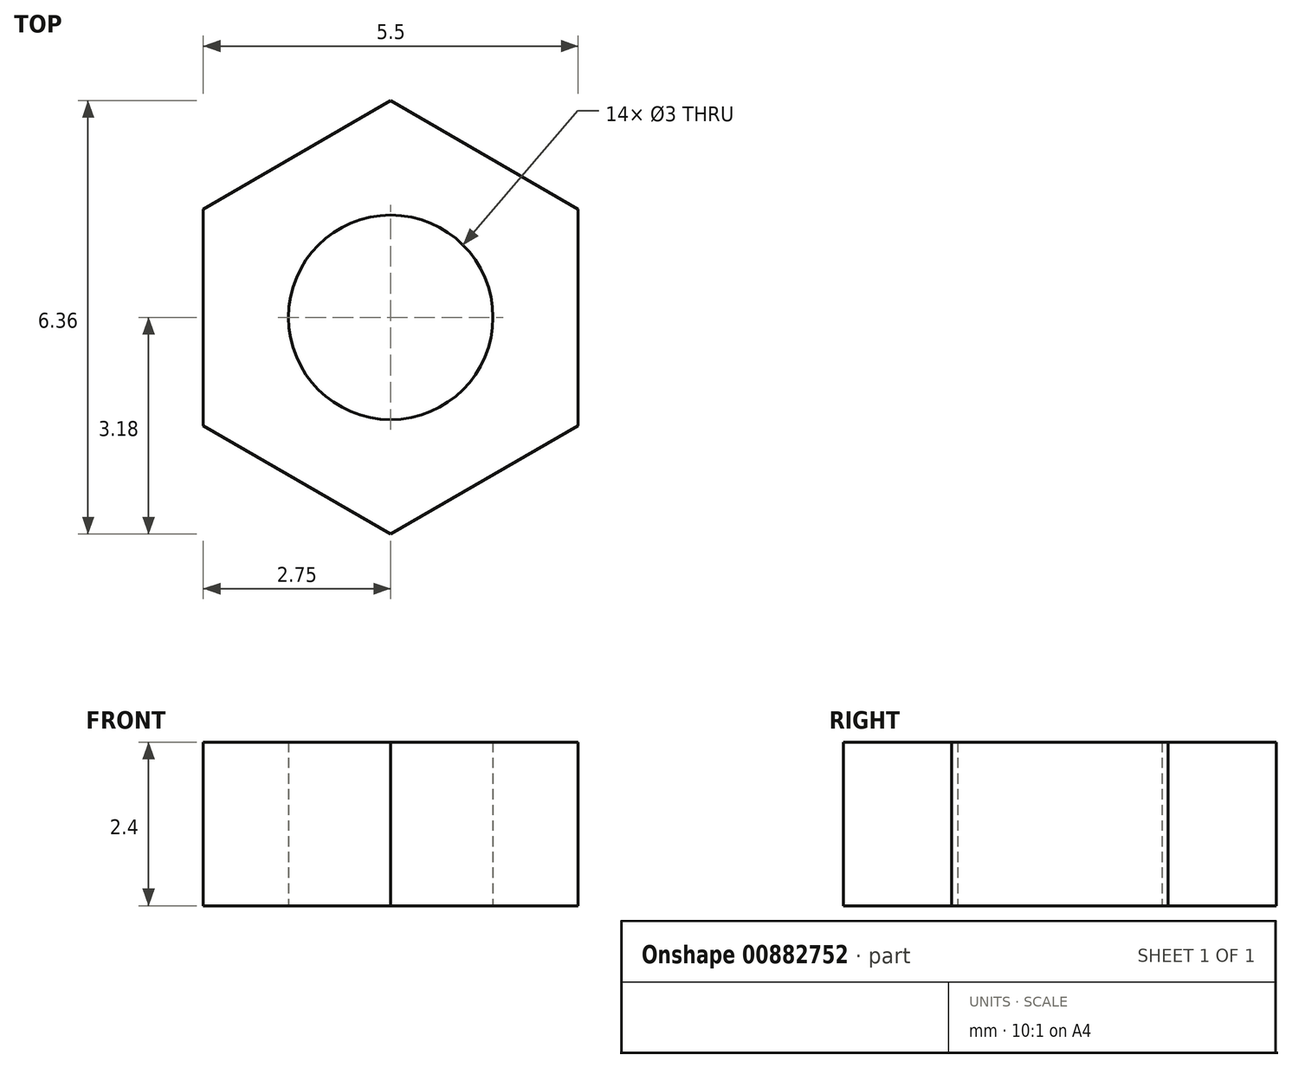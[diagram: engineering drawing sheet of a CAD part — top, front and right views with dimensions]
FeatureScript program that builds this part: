
annotation { "Feature Type Name" : "Feature", "Feature Type Description" : "" }
export const myFeature = defineFeature(function(context is Context, id is Id, definition is map)
    precondition{}
    {
        {
            var Q0;
            Q0=qCreatedBy(makeId("Top.planeOp"),FACE);
            var sketch = newSketch(context, id + "F0", { "sketchPlane" : qUnion([Q0])});
            skCircle(sketch, "E0", {"center": v(0, 0) * mm, "radius": 1.5 * mm});
            skCircle(sketch, "E1", {"center": v(0, 0) * mm, "radius": 2.75 * mm});
            skCircle(sketch, "E2.cCircle", {"center": v(0, 0) * mm, "radius": 2.75 * mm, "construction": true});
            skLineSegment(sketch, "E2.0", {"start": v(2.75, 1.59) * mm, "end": v(2.75, -1.59) * mm});
            skLineSegment(sketch, "E2.1", {"start": v(2.75, -1.59) * mm, "end": v(0, -3.18) * mm});
            skLineSegment(sketch, "E2.2", {"start": v(0, -3.18) * mm, "end": v(-2.75, -1.59) * mm});
            skLineSegment(sketch, "E2.3", {"start": v(-2.75, -1.59) * mm, "end": v(-2.75, 1.59) * mm});
            skLineSegment(sketch, "E2.4", {"start": v(-2.75, 1.59) * mm, "end": v(0, 3.18) * mm});
            skLineSegment(sketch, "E2.5", {"start": v(0, 3.18) * mm, "end": v(2.75, 1.59) * mm});
            skPoint(sketch, "E2.0.midPoint", {"position": v(2.75, 0) * mm});
            skSolve(sketch);
        }
        {
            var Q0;
            Q0 = qSketchRegion(id + "F0", true);
            extrude(context, id + "F1", {"entities" : qUnion([Q0]), "depth" : 2.4 * mm, "offsetDistance" : 25 * mm});
        }
    });
